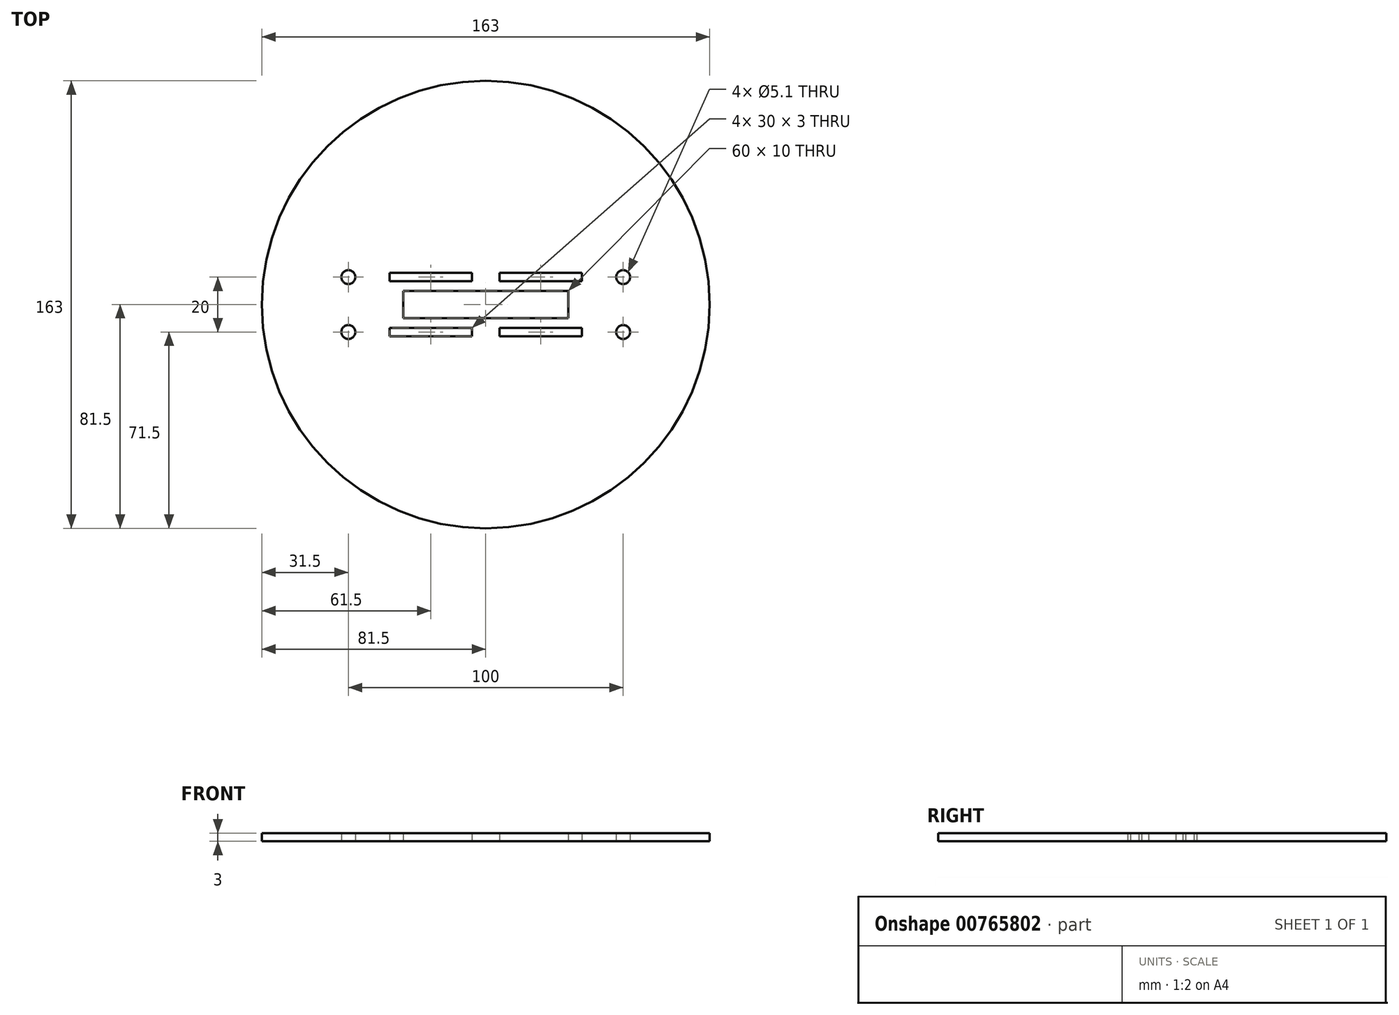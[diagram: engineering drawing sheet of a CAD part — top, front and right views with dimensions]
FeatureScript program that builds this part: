
annotation { "Feature Type Name" : "Feature", "Feature Type Description" : "" }
export const myFeature = defineFeature(function(context is Context, id is Id, definition is map)
    precondition{}
    {
        {
            var Q0;
            Q0=qCreatedBy(makeId("Top.planeOp"),FACE);
            var sketch = newSketch(context, id + "F0", { "sketchPlane" : qUnion([Q0])});
            skCircle(sketch, "E0", {"center": v(0, 0) * mm, "radius": 81.5 * mm});
            skLineSegment(sketch, "E1.bottom", {"start": v(50, 10) * mm, "end": v(-50, 10) * mm, "construction": true});
            skLineSegment(sketch, "E1.top", {"start": v(50, -10) * mm, "end": v(-50, -10) * mm, "construction": true});
            skLineSegment(sketch, "E1.left", {"start": v(50, 10) * mm, "end": v(50, -10) * mm, "construction": true});
            skLineSegment(sketch, "E1.right", {"start": v(-50, 10) * mm, "end": v(-50, -10) * mm, "construction": true});
            skCircle(sketch, "E2", {"center": v(-50, 10) * mm, "radius": 2.55 * mm});
            skCircle(sketch, "E3", {"center": v(50, 10) * mm, "radius": 2.55 * mm});
            skCircle(sketch, "E4", {"center": v(50, -10) * mm, "radius": 2.55 * mm});
            skCircle(sketch, "E5", {"center": v(-50, -10) * mm, "radius": 2.55 * mm});
            skLineSegment(sketch, "E6.bottom", {"start": v(-5, 11.5) * mm, "end": v(-35, 11.5) * mm});
            skLineSegment(sketch, "E6.top", {"start": v(-5, 8.5) * mm, "end": v(-35, 8.5) * mm});
            skLineSegment(sketch, "E6.left", {"start": v(-5, 11.5) * mm, "end": v(-5, 8.5) * mm});
            skLineSegment(sketch, "E6.right", {"start": v(-35, 11.5) * mm, "end": v(-35, 8.5) * mm});
            skPoint(sketch, "E6.middle", {"position": v(-20, 10) * mm});
            skLineSegment(sketch, "E7.MirrorCS", {"start": v(5, 11.5) * mm, "end": v(5, 8.5) * mm});
            skLineSegment(sketch, "E8.MirrorCS", {"start": v(35, 11.5) * mm, "end": v(35, 8.5) * mm});
            skLineSegment(sketch, "E9.MirrorCS", {"start": v(5, 11.5) * mm, "end": v(35, 11.5) * mm});
            skLineSegment(sketch, "E10.MirrorCS", {"start": v(5, 8.5) * mm, "end": v(35, 8.5) * mm});
            skPoint(sketch, "E11.MirrorP", {"position": v(20, 10) * mm});
            skLineSegment(sketch, "E12.MirrorCS", {"start": v(5, -11.5) * mm, "end": v(5, -8.5) * mm});
            skLineSegment(sketch, "E13.MirrorCS", {"start": v(35, -11.5) * mm, "end": v(35, -8.5) * mm});
            skLineSegment(sketch, "E14.MirrorCS", {"start": v(-35, -11.5) * mm, "end": v(-35, -8.5) * mm});
            skLineSegment(sketch, "E15.MirrorCS", {"start": v(-5, -11.5) * mm, "end": v(-5, -8.5) * mm});
            skLineSegment(sketch, "E16.MirrorCS", {"start": v(5, -8.5) * mm, "end": v(35, -8.5) * mm});
            skLineSegment(sketch, "E17.MirrorCS", {"start": v(5, -11.5) * mm, "end": v(35, -11.5) * mm});
            skPoint(sketch, "E18.MirrorP", {"position": v(20, -10) * mm});
            skPoint(sketch, "E19.MirrorP", {"position": v(-20, -10) * mm});
            skLineSegment(sketch, "E20.MirrorCS", {"start": v(-5, -11.5) * mm, "end": v(-35, -11.5) * mm});
            skLineSegment(sketch, "E21.MirrorCS", {"start": v(-5, -8.5) * mm, "end": v(-35, -8.5) * mm});
            skLineSegment(sketch, "E22.bottom", {"start": v(30, 5) * mm, "end": v(-30, 5) * mm});
            skLineSegment(sketch, "E22.top", {"start": v(30, -5) * mm, "end": v(-30, -5) * mm});
            skLineSegment(sketch, "E22.left", {"start": v(30, 5) * mm, "end": v(30, -5) * mm});
            skLineSegment(sketch, "E22.right", {"start": v(-30, 5) * mm, "end": v(-30, -5) * mm});
            skSolve(sketch);
        }
        {
            var Q0;
            Q0=makeQuery(id+"F0.imprint","IMPRINT",FACE,{"disambiguationData":[TD([[makeQuery(id+"F0.imprint","IMPRINT",EDGE,{"derivedFrom":sQuery(id+"F0.wireOp",EDGE,"E0")}),1.0]])]});
            var Q1;
            Q1=makeQuery(id+"F0.imprint","IMPRINT",FACE,{"disambiguationData":[TD([[makeQuery(id+"F0.imprint","IMPRINT",EDGE,{"derivedFrom":sQuery(id+"F0.wireOp",EDGE,"12f80adc-9bbd-4cf1-b3ab-28a8661f77270.MirrorC")}),1.0]])]});
            var Q2;
            Q2=makeQuery(id+"F0.imprint","IMPRINT",FACE,{"disambiguationData":[TD([[makeQuery(id+"F0.imprint","IMPRINT",EDGE,{"derivedFrom":sQuery(id+"F0.wireOp",EDGE,"V9Knnmj0-hhsS-TjCZ-my9t-nB7dD1luZK0G")}),1.0]])]});
            extrude(context, id + "F1", {"entities" : qUnion([Q0, Q1, Q2]), "depth" : 3 * mm, "offsetDistance" : 25 * mm});
        }
    });
